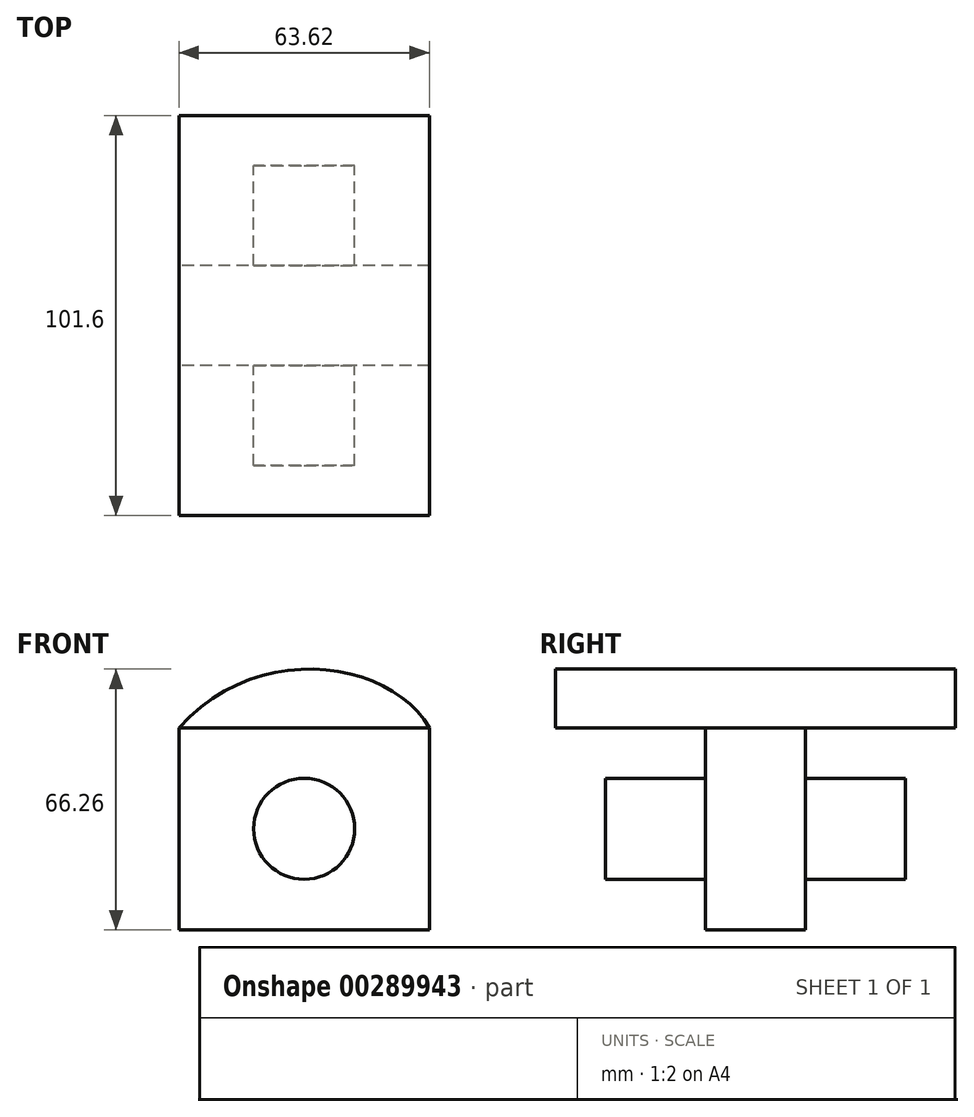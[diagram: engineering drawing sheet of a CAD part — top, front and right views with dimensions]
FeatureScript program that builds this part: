
annotation { "Feature Type Name" : "Feature", "Feature Type Description" : "" }
export const myFeature = defineFeature(function(context is Context, id is Id, definition is map)
    precondition{}
    {
        {
            var Q0;
            Q0=qCreatedBy(makeId("Front.planeOp"),FACE);
            var sketch = newSketch(context, id + "F0", { "sketchPlane" : qUnion([Q0])});
            skLineSegment(sketch, "E0.bottom", {"start": v(31.81, 25.68) * mm, "end": v(-31.81, 25.68) * mm});
            skLineSegment(sketch, "E0.top", {"start": v(31.81, -25.68) * mm, "end": v(-31.81, -25.68) * mm});
            skLineSegment(sketch, "E0.left", {"start": v(31.81, 25.68) * mm, "end": v(31.81, -25.68) * mm});
            skLineSegment(sketch, "E0.right", {"start": v(-31.81, 25.68) * mm, "end": v(-31.81, -25.68) * mm});
            skPoint(sketch, "E0.middle", {"position": v(0, 0) * mm});
            skCircle(sketch, "E1", {"center": v(0, 0) * mm, "radius": 12.83 * mm});
            skFitSpline(sketch, "E2", {"points": [v(-31.81, 25.68) * mm, v(31.81, 25.68) * mm], "startDerivative": vector(60.88, 67.86) * mm, "endDerivative": vector(29.17, -50.73) * mm});
            skSolve(sketch);
        }
        {
            var Q0;
            Q0=makeQuery(id+"F0.imprint","IMPRINT",FACE,{"disambiguationData":[TD([[makeQuery(id+"F0.imprint","IMPRINT",EDGE,{"derivedFrom":sQuery(id+"F0.wireOp",EDGE,"E0.bottom")}),1.0]])]});
            extrude(context, id + "F1", {"entities" : qUnion([Q0]), "endBound" : BoundingType.SYMMETRIC, "depth" : 25.4 * mm});
        }
        {
            var Q0;
            Q0=makeQuery(id+"F0.imprint","IMPRINT",FACE,{"disambiguationData":[TD([[makeQuery(id+"F0.imprint","IMPRINT",EDGE,{"derivedFrom":sQuery(id+"F0.wireOp",EDGE,"E0.bottom")}),-1.0]])]});
            extrude(context, id + "F2", {"entities" : qUnion([Q0]), "operationType" : NewBodyOperationType.ADD, "endBound" : BoundingType.SYMMETRIC, "depth" : 101.6 * mm});
        }
        {
            var Q0;
            Q0=makeQuery(id+"F0.imprint","IMPRINT",FACE,{"disambiguationData":[TD([[makeQuery(id+"F0.imprint","IMPRINT",EDGE,{"derivedFrom":sQuery(id+"F0.wireOp",EDGE,"E1")}),1.0]])]});
            extrude(context, id + "F3", {"entities" : qUnion([Q0]), "operationType" : NewBodyOperationType.ADD, "endBound" : BoundingType.SYMMETRIC, "depth" : 76.2 * mm});
        }
    });
